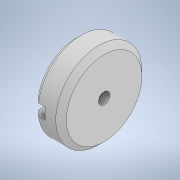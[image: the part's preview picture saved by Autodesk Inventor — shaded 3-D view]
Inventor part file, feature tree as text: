
AUTODESK INVENTOR PART (.ipt)
format: ipt  version: 2022 (Build 260153000, 153)  size: 142,336 bytes
history: native  units: mm
features: sketch x3, revolve x2, other x1, extrude x1
ambient origin geometry x8: Origin, YZ Plane, XZ Plane, XY Plane, X Axis, Y Axis, Z Axis, Center Point
bodies: Body1 (feature_tree)
feature tree (7):
  other  "Твердое тело1"
  revolve  "Вращение1"
  revolve  "Вращение2"
  extrude  "Выдавливание1"  Depth=20.0mm
  sketch  "Эскиз1"
  sketch  "Эскиз2"
  sketch  "Эскиз3"
